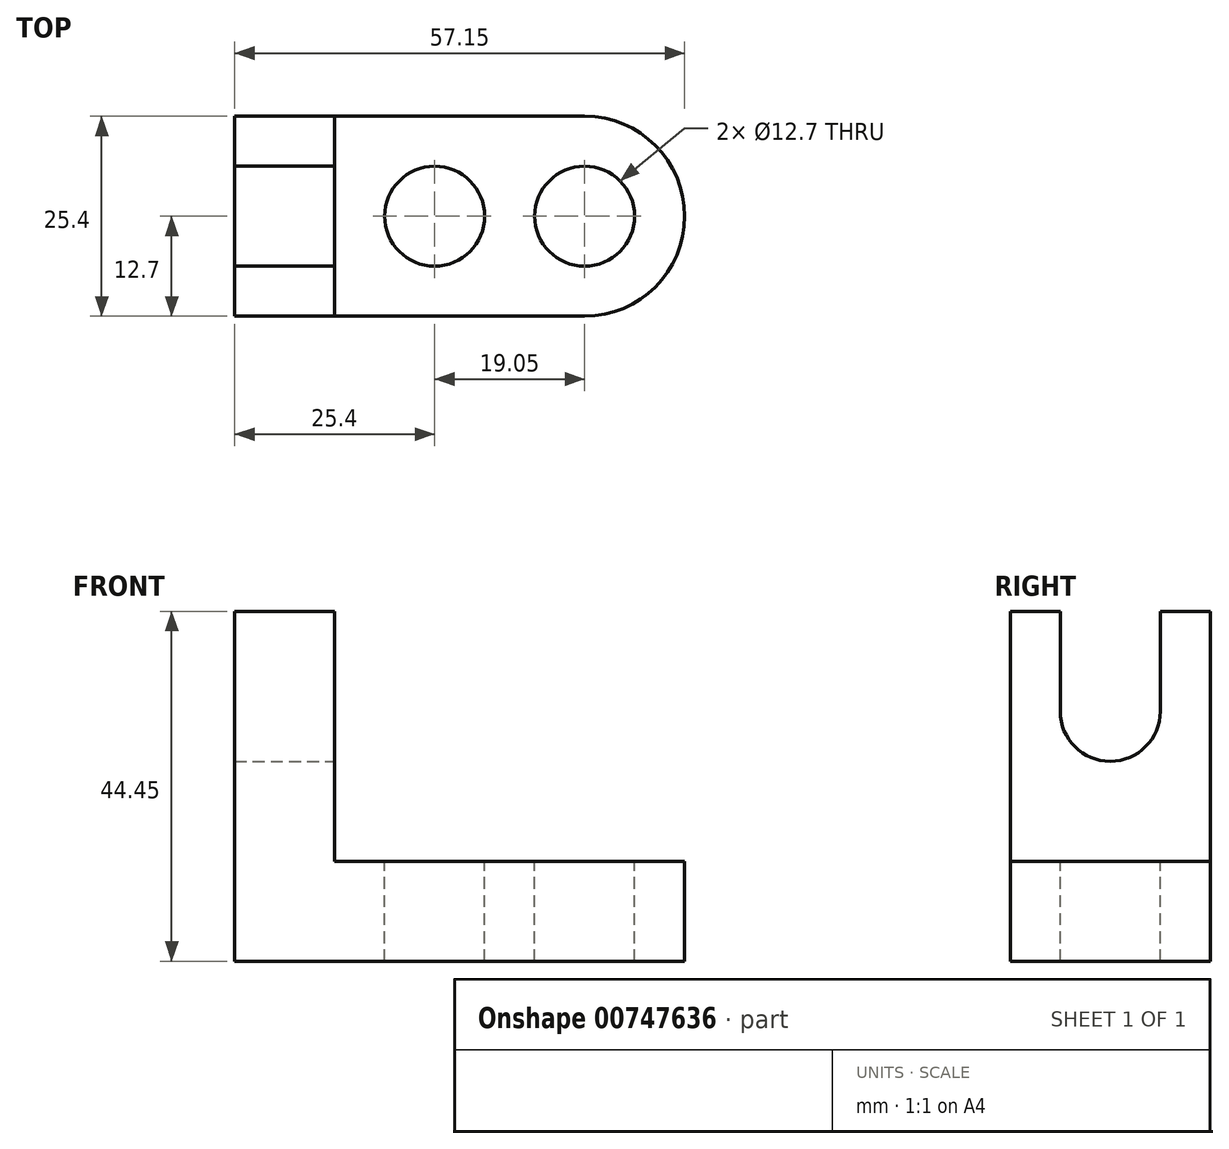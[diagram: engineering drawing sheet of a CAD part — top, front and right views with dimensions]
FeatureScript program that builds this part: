
annotation { "Feature Type Name" : "Feature", "Feature Type Description" : "" }
export const myFeature = defineFeature(function(context is Context, id is Id, definition is map)
    precondition{}
    {
        {
            var Q0;
            Q0=qCreatedBy(makeId("Front.planeOp"),FACE);
            var sketch = newSketch(context, id + "F0", { "sketchPlane" : qUnion([Q0])});
            skLineSegment(sketch, "E0", {"start": v(0, 0) * mm, "end": v(63.5, 0) * mm});
            skLineSegment(sketch, "E1", {"start": v(63.5, 0) * mm, "end": v(63.5, 44.45) * mm});
            skLineSegment(sketch, "E2", {"start": v(63.5, 44.45) * mm, "end": v(0, 44.45) * mm});
            skLineSegment(sketch, "E3", {"start": v(0, 44.45) * mm, "end": v(0, 0) * mm});
            skSolve(sketch);
        }
        {
            var Q0;
            Q0=makeQuery(id+"F0.imprint","IMPRINT",FACE,{"disambiguationData":[TD([[makeQuery(id+"F0.imprint","IMPRINT",EDGE,{"derivedFrom":sQuery(id+"F0.wireOp",EDGE,"E0")}),1.0]])]});
            extrude(context, id + "F1", {"entities" : qUnion([Q0]), "oppositeDirection" : true, "depth" : 25.4 * mm, "offsetDistance" : 25.4 * mm});
        }
        {
            var Q0;
            Q0=makeQuery(id+"F1.opExtrude","SWEPT_FACE",FACE,{"disambiguationData":[OSD([sQuery(id+"F0.wireOp",EDGE,"E1")])]});
            extrude(context, id + "F2", {"entities" : qUnion([Q0]), "operationType" : NewBodyOperationType.REMOVE, "oppositeDirection" : true, "depth" : 6.35 * mm, "offsetDistance" : 25.4 * mm});
        }
        {
            var Q0;
            Q0=makeQuery(id+"F1.opExtrude","CAP_FACE",FACE,{"disambiguationData":[OSD([sQuery(id+"F0.wireOp",EDGE,"E0"),sQuery(id+"F0.wireOp",EDGE,"E1"),sQuery(id+"F0.wireOp",EDGE,"E2"),sQuery(id+"F0.wireOp",EDGE,"E3")])],"isStart":true});
            var sketch = newSketch(context, id + "F3", { "sketchPlane" : qUnion([Q0])});
            skLineSegment(sketch, "E4", {"start": v(12.7, 44.45) * mm, "end": v(12.7, 12.7) * mm});
            skLineSegment(sketch, "E5", {"start": v(12.7, 12.7) * mm, "end": v(57.15, 12.7) * mm});
            skSolve(sketch);
        }
        {
            var Q0;
            {var subQ0=sQuery(id+"F3.wireOp",EDGE,"E4");Q0=makeQuery(id+"F3.imprint","IMPRINT",FACE,{"disambiguationData":[TD([[makeQuery(id+"F3.imprint","IMPRINT",EDGE,{"derivedFrom":subQ0}),1.0]])]});}
            extrude(context, id + "F4", {"entities" : qUnion([Q0]), "operationType" : NewBodyOperationType.REMOVE, "oppositeDirection" : true, "depth" : 25.4 * mm, "offsetDistance" : 25.4 * mm});
        }
        {
            var Q0;
            Q0=makeQuery(id+"F4.boolean.opBoolean","COPY",FACE,{"derivedFrom":makeQuery(id+"F4.opExtrude","SWEPT_FACE",FACE,{"disambiguationData":[OSD([sQuery(id+"F3.wireOp",EDGE,"E5")])]})});
            var sketch = newSketch(context, id + "F5", { "sketchPlane" : qUnion([Q0])});
            skCircle(sketch, "E6", {"center": v(25.4, 12.7) * mm, "radius": 6.35 * mm});
            skPoint(sketch, "E6.centerSnap0", {"position": v(12.7, 12.7) * mm});
            skCircle(sketch, "E7", {"center": v(44.45, 12.7) * mm, "radius": 6.35 * mm});
            skSolve(sketch);
        }
        {
            var Q0;
            Q0 = qSketchRegion(id + "F5", true);
            extrude(context, id + "F6", {"entities" : qUnion([Q0]), "operationType" : NewBodyOperationType.REMOVE, "oppositeDirection" : true, "depth" : 25.4 * mm, "offsetDistance" : 25.4 * mm});
        }
        {
            var Q0;
            Q0=makeQuery(id+"F4.boolean.opBoolean","COPY",FACE,{"derivedFrom":makeQuery(id+"F4.opExtrude","SWEPT_FACE",FACE,{"disambiguationData":[OSD([sQuery(id+"F3.wireOp",EDGE,"E5")])]})});
            var sketch = newSketch(context, id + "F7", { "sketchPlane" : qUnion([Q0])});
            skArc(sketch, "E8", {"start": v(44.45, 0) * mm, "mid": v(57.15, 12.7) * mm, "end": v(44.45, 25.4) * mm});
            skSolve(sketch);
        }
        {
            var Q0;
            Q0 = qSketchRegion(id + "F7", true);
            var Q1;
            {var subQ0=sQuery(id+"F7.wireOp",EDGE,"E8");var subQ1=sQuery(id+"F3.wireOp",EDGE,"E5");var subQ2=makeQuery(id+"F4.boolean.opBoolean","COPY",EDGE,{"derivedFrom":makeQuery(id+"F4.opExtrude","CAP_EDGE",EDGE,{"disambiguationData":[OSD([subQ1])],"isStart":false})});var subQ3=makeQuery(id+"F7.imprint","INTERSECT",VERTEX,{"derivedFrom":[subQ2,subQ0]});Q1=makeQuery(id+"F7.imprint","IMPRINT",FACE,{"disambiguationData":[TD([[makeQuery(id+"F7.imprint","IMPRINT",EDGE,{"disambiguationData":[TD([[subQ3,1.0]])],"derivedFrom":subQ0}),-1.0]])]});}
            var Q2;
            {var subQ0=sQuery(id+"F7.wireOp",EDGE,"E8");var subQ1=sQuery(id+"F3.wireOp",EDGE,"E5");var subQ2=makeQuery(id+"F4.boolean.opBoolean","COPY",EDGE,{"derivedFrom":makeQuery(id+"F4.opExtrude","CAP_EDGE",EDGE,{"disambiguationData":[OSD([subQ1])],"isStart":true})});var subQ3=makeQuery(id+"F7.imprint","INTERSECT",VERTEX,{"derivedFrom":[subQ2,subQ0]});Q2=makeQuery(id+"F7.imprint","IMPRINT",FACE,{"disambiguationData":[TD([[makeQuery(id+"F7.imprint","IMPRINT",EDGE,{"disambiguationData":[TD([[subQ3,-1.0]])],"derivedFrom":subQ0}),-1.0]])]});}
            extrude(context, id + "F8", {"entities" : qUnion([Q0, Q1, Q2]), "operationType" : NewBodyOperationType.REMOVE, "oppositeDirection" : true, "depth" : 25.4 * mm, "offsetDistance" : 25.4 * mm});
        }
        {
            var Q0;
            Q0=makeQuery(id+"F4.boolean.opBoolean","COPY",FACE,{"derivedFrom":makeQuery(id+"F4.opExtrude","SWEPT_FACE",FACE,{"disambiguationData":[OSD([sQuery(id+"F3.wireOp",EDGE,"E4")])]})});
            var sketch = newSketch(context, id + "F9", { "sketchPlane" : qUnion([Q0])});
            skCircle(sketch, "E9", {"center": v(12.7, 31.75) * mm, "radius": 6.35 * mm});
            skLineSegment(sketch, "E10", {"start": v(19.05, 31.75) * mm, "end": v(19.05, 44.45) * mm});
            skLineSegment(sketch, "E11", {"start": v(6.35, 31.75) * mm, "end": v(6.35, 44.45) * mm});
            skArc(sketch, "E12", {"start": v(25.4, 38.1) * mm, "mid": v(12.7, 44.45) * mm, "end": v(0, 38.1) * mm});
            skPoint(sketch, "E12.startSnap0", {"position": v(6.35, 38.1) * mm});
            skPoint(sketch, "E12.endSnap0", {"position": v(6.35, 38.1) * mm});
            skSolve(sketch);
        }
        {
            var Q0;
            {var subQ0=sQuery(id+"F9.wireOp",EDGE,"E10");var subQ3=sQuery(id+"F9.wireOp",EDGE,"E12");var subQ4=makeQuery(id+"F9.imprint","INTERSECT",VERTEX,{"derivedFrom":[subQ0,subQ3]});Q0=makeQuery(id+"F9.imprint","IMPRINT",FACE,{"disambiguationData":[TD([[makeQuery(id+"F9.imprint","IMPRINT",EDGE,{"disambiguationData":[TD([[subQ4,-1.0]])],"derivedFrom":subQ0}),1.0]])]});}
            var Q1;
            {var subQ0=sQuery(id+"F9.wireOp",EDGE,"E11");var subQ3=sQuery(id+"F9.wireOp",EDGE,"E12");var subQ4=makeQuery(id+"F9.imprint","INTERSECT",VERTEX,{"derivedFrom":[subQ0,subQ3]});Q1=makeQuery(id+"F9.imprint","IMPRINT",FACE,{"disambiguationData":[TD([[makeQuery(id+"F9.imprint","IMPRINT",EDGE,{"disambiguationData":[TD([[subQ4,-1.0]])],"derivedFrom":subQ0}),-1.0]])]});}
            var Q2;
            {var subQ1=sQuery(id+"F3.wireOp",EDGE,"E4");var subQ4=sQuery(id+"F9.wireOp",EDGE,"E12");var subQ6=makeQuery(id+"F4.boolean.opBoolean","COPY",EDGE,{"derivedFrom":makeQuery(id+"F4.opExtrude","CAP_EDGE",EDGE,{"disambiguationData":[OSD([subQ1])],"isStart":true})});var subQ8=makeQuery(id+"F9.imprint","INTERSECT",VERTEX,{"derivedFrom":[subQ6,subQ4]});Q2=makeQuery(id+"F9.imprint","IMPRINT",FACE,{"disambiguationData":[TD([[makeQuery(id+"F9.imprint","IMPRINT",EDGE,{"disambiguationData":[TD([[subQ8,1.0]])],"derivedFrom":subQ4}),-1.0]])]});}
            var Q3;
            {var subQ0=sQuery(id+"F9.wireOp",EDGE,"E9");var subQ1=makeQuery(id+"F9.imprint","INTERSECT",VERTEX,{"derivedFrom":[subQ0,sQuery(id+"F9.wireOp",EDGE,"E10")]});Q3=makeQuery(id+"F9.imprint","IMPRINT",FACE,{"disambiguationData":[TD([[makeQuery(id+"F9.imprint","IMPRINT",EDGE,{"disambiguationData":[TD([[subQ1,-1.0]])],"derivedFrom":subQ0}),1.0]])]});}
            var Q4;
            {var subQ1=sQuery(id+"F9.wireOp",EDGE,"E9");var subQ5=sQuery(id+"F9.wireOp",EDGE,"E10");var subQ8=makeQuery(id+"F9.imprint","INTERSECT",VERTEX,{"derivedFrom":[subQ1,subQ5]});Q4=makeQuery(id+"F9.imprint","IMPRINT",FACE,{"disambiguationData":[TD([[makeQuery(id+"F9.imprint","IMPRINT",EDGE,{"disambiguationData":[TD([[subQ8,-1.0]])],"derivedFrom":subQ1}),-1.0]])]});}
            var Q5;
            {var subQ1=sQuery(id+"F3.wireOp",EDGE,"E4");var subQ4=sQuery(id+"F9.wireOp",EDGE,"E12");var subQ6=makeQuery(id+"F4.boolean.opBoolean","COPY",EDGE,{"derivedFrom":makeQuery(id+"F4.opExtrude","CAP_EDGE",EDGE,{"disambiguationData":[OSD([subQ1])],"isStart":false})});var subQ7=makeQuery(id+"F9.imprint","INTERSECT",VERTEX,{"derivedFrom":[subQ6,subQ4]});Q5=makeQuery(id+"F9.imprint","IMPRINT",FACE,{"disambiguationData":[TD([[makeQuery(id+"F9.imprint","IMPRINT",EDGE,{"disambiguationData":[TD([[subQ7,-1.0]])],"derivedFrom":subQ4}),-1.0]])]});}
            extrude(context, id + "F10", {"entities" : qUnion([Q0, Q1, Q2, Q3, Q4, Q5]), "operationType" : NewBodyOperationType.REMOVE, "oppositeDirection" : true, "depth" : 25.4 * mm, "offsetDistance" : 25.4 * mm});
        }
    });
